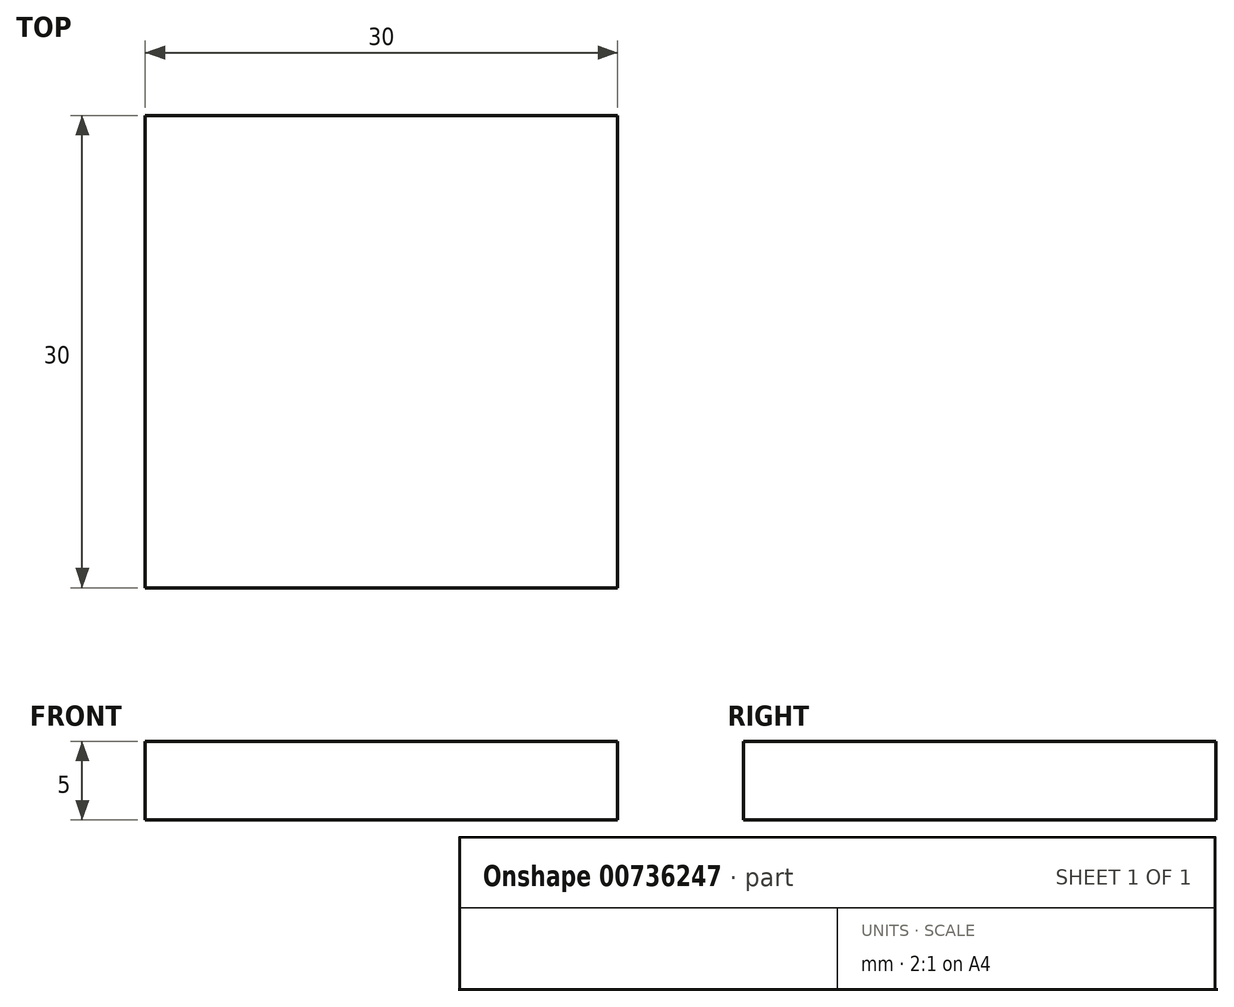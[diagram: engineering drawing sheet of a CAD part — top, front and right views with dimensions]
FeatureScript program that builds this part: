
annotation { "Feature Type Name" : "Feature", "Feature Type Description" : "" }
export const myFeature = defineFeature(function(context is Context, id is Id, definition is map)
    precondition{}
    {
        {
            var Q0;
            Q0=qCreatedBy(makeId("Top.planeOp"),FACE);
            var sketch = newSketch(context, id + "F0", { "sketchPlane" : qUnion([Q0])});
            skLineSegment(sketch, "E0.bottom", {"start": v(-15, 15) * mm, "end": v(15, 15) * mm});
            skLineSegment(sketch, "E0.top", {"start": v(-15, -15) * mm, "end": v(15, -15) * mm});
            skLineSegment(sketch, "E0.left", {"start": v(-15, 15) * mm, "end": v(-15, -15) * mm});
            skLineSegment(sketch, "E0.right", {"start": v(15, 15) * mm, "end": v(15, -15) * mm});
            skPoint(sketch, "E0.middle", {"position": v(0, 0) * mm});
            skSolve(sketch);
        }
        {
            var Q0;
            Q0 = qSketchRegion(id + "F0", true);
            extrude(context, id + "F1", {"entities" : qUnion([Q0]), "depth" : 5 * mm, "offsetDistance" : 25 * mm});
        }
    });
